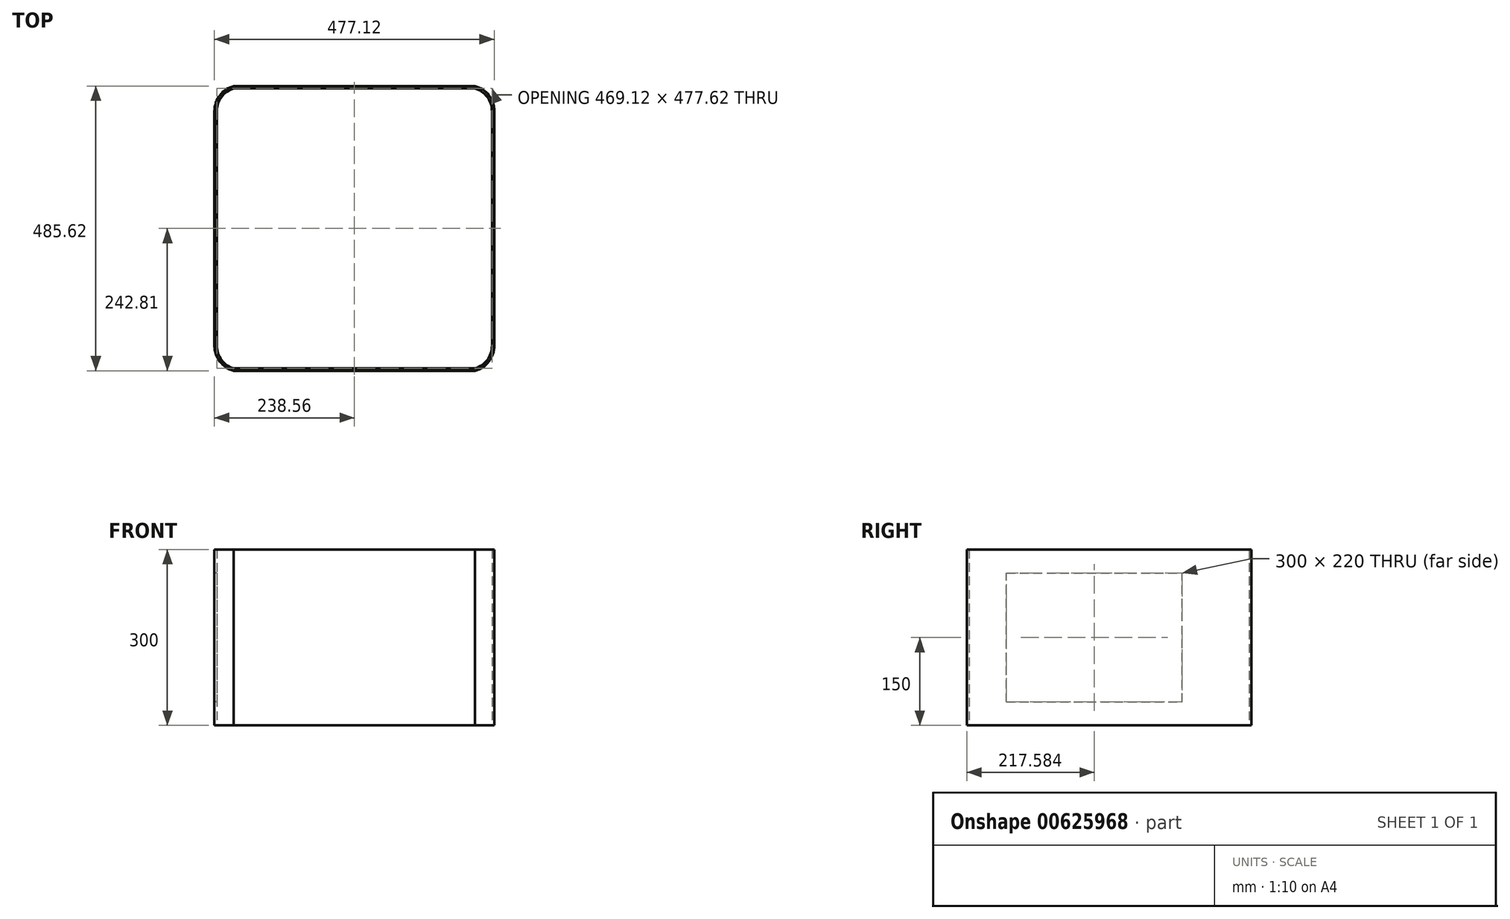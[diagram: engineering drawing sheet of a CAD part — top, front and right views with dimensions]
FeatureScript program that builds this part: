
annotation { "Feature Type Name" : "Feature", "Feature Type Description" : "" }
export const myFeature = defineFeature(function(context is Context, id is Id, definition is map)
    precondition{}
    {
        {
            var Q0;
            Q0=qCreatedBy(makeId("Top.planeOp"),FACE);
            var sketch = newSketch(context, id + "F0", { "sketchPlane" : qUnion([Q0])});
            skLineSegment(sketch, "E0.bottom", {"start": v(-205.64, 242.8) * mm, "end": v(205.63, 242.8) * mm});
            skLineSegment(sketch, "E0.top", {"start": v(-205.64, -242.8) * mm, "end": v(205.63, -242.8) * mm});
            skLineSegment(sketch, "E0.left", {"start": v(-238.56, 200.23) * mm, "end": v(-238.56, -200.23) * mm});
            skLineSegment(sketch, "E0.right", {"start": v(238.56, 200.23) * mm, "end": v(238.56, -200.23) * mm});
            skLineSegment(sketch, "E1", {"start": v(-205.64, 242.8) * mm, "end": v(205.63, 242.8) * mm, "construction": true});
            skLineSegment(sketch, "E2", {"start": v(-238.56, 200.23) * mm, "end": v(-238.56, -200.23) * mm, "construction": true});
            skLineSegment(sketch, "E3.MirrorCS", {"start": v(238.56, 200.23) * mm, "end": v(238.56, -200.23) * mm, "construction": true});
            skLineSegment(sketch, "E4.MirrorCS", {"start": v(-205.64, -242.8) * mm, "end": v(205.63, -242.8) * mm, "construction": true});
            skArc(sketch, "E5", {"start": v(-205.64, 242.8) * mm, "mid": v(-229.37, 227.14) * mm, "end": v(-238.56, 200.23) * mm});
            skArc(sketch, "E6", {"start": v(238.56, 200.23) * mm, "mid": v(229.37, 227.14) * mm, "end": v(205.63, 242.8) * mm});
            skArc(sketch, "E7", {"start": v(-238.56, -200.23) * mm, "mid": v(-229.37, -227.14) * mm, "end": v(-205.64, -242.8) * mm});
            skArc(sketch, "E8", {"start": v(205.63, -242.8) * mm, "mid": v(229.37, -227.14) * mm, "end": v(238.56, -200.23) * mm});
            skPoint(sketch, "E9.orphan", {"position": v(-238.56, 242.8) * mm});
            skPoint(sketch, "E10.orphan", {"position": v(-238.56, -242.8) * mm});
            skSolve(sketch);
        }
        {
            var Q0;
            Q0=makeQuery(id+"F0.imprint","IMPRINT",FACE,{"disambiguationData":[TD([[makeQuery(id+"F0.imprint","IMPRINT",EDGE,{"derivedFrom":sQuery(id+"F0.wireOp",EDGE,"E0.bottom")}),-1.0]])]});
            extrude(context, id + "F1", {"entities" : qUnion([Q0]), "depth" : 300 * mm, "offsetDistance" : 25 * mm});
        }
        {
            var Q0;
            Q0=makeQuery(id+"F1.opExtrude","CAP_FACE",FACE,{"disambiguationData":[OSD([sQuery(id+"F0.wireOp",EDGE,"E0.bottom"),sQuery(id+"F0.wireOp",EDGE,"E0.top"),sQuery(id+"F0.wireOp",EDGE,"E0.left"),sQuery(id+"F0.wireOp",EDGE,"E0.right"),sQuery(id+"F0.wireOp",EDGE,"E5"),sQuery(id+"F0.wireOp",EDGE,"E6"),sQuery(id+"F0.wireOp",EDGE,"E7"),sQuery(id+"F0.wireOp",EDGE,"E8")])],"isStart":true});
            shell(context, id + "F2", {"entities" : qUnion([Q0]), "thickness" : 4 * mm});
        }
        {
            var Q0;
            Q0=makeQuery(id+"F2.opShell","OFFSET_FACE",FACE,{"disambiguationData":[OSD([sQuery(id+"F0.wireOp",EDGE,"E0.bottom"),sQuery(id+"F0.wireOp",EDGE,"E0.top"),sQuery(id+"F0.wireOp",EDGE,"E0.left"),sQuery(id+"F0.wireOp",EDGE,"E0.right"),sQuery(id+"F0.wireOp",EDGE,"E5"),sQuery(id+"F0.wireOp",EDGE,"E6"),sQuery(id+"F0.wireOp",EDGE,"E7"),sQuery(id+"F0.wireOp",EDGE,"E8")])]});
            var sketch = newSketch(context, id + "F3", { "sketchPlane" : qUnion([Q0])});
            skLineSegment(sketch, "E11", {"start": v(-234.56, 200.23) * mm, "end": v(-234.56, -200.23) * mm});
            skArc(sketch, "E12", {"start": v(-234.56, -200.23) * mm, "mid": v(-226.36, -224.5) * mm, "end": v(-205.11, -238.8) * mm});
            skLineSegment(sketch, "E13", {"start": v(-205.11, -238.8) * mm, "end": v(205.11, -238.8) * mm});
            skArc(sketch, "E14", {"start": v(205.11, -238.8) * mm, "mid": v(226.36, -224.5) * mm, "end": v(234.56, -200.23) * mm});
            skLineSegment(sketch, "E15", {"start": v(234.56, -200.23) * mm, "end": v(234.56, 200.23) * mm});
            skArc(sketch, "E16", {"start": v(234.56, 200.23) * mm, "mid": v(226.36, 224.5) * mm, "end": v(205.11, 238.8) * mm});
            skLineSegment(sketch, "E17", {"start": v(205.11, 238.8) * mm, "end": v(-205.11, 238.8) * mm});
            skArc(sketch, "E18", {"start": v(-205.11, 238.8) * mm, "mid": v(-226.36, 224.5) * mm, "end": v(-234.56, 200.23) * mm});
            skSolve(sketch);
        }
        {
            var Q0;
            Q0=makeQuery(id+"F3.imprint","IMPRINT",FACE,{"disambiguationData":[TD([[makeQuery(id+"F3.imprint","IMPRINT",EDGE,{"derivedFrom":sQuery(id+"F3.wireOp",EDGE,"E11")}),-1.0]])]});
            extrude(context, id + "F4", {"entities" : qUnion([Q0]), "operationType" : NewBodyOperationType.REMOVE, "oppositeDirection" : true, "depth" : 25 * mm, "offsetDistance" : 25 * mm});
        }
        {
            var Q0;
            Q0=makeQuery(id+"F1.opExtrude","SWEPT_FACE",FACE,{"disambiguationData":[OSD([sQuery(id+"F0.wireOp",EDGE,"E0.left")])]});
            var sketch = newSketch(context, id + "F5", { "sketchPlane" : qUnion([Q0])});
            skLineSegment(sketch, "E19.bottom", {"start": v(175.23, 40) * mm, "end": v(-124.77, 40) * mm});
            skLineSegment(sketch, "E19.top", {"start": v(175.23, 260) * mm, "end": v(-124.77, 260) * mm});
            skLineSegment(sketch, "E19.left", {"start": v(175.23, 40) * mm, "end": v(175.23, 260) * mm});
            skLineSegment(sketch, "E19.right", {"start": v(-124.77, 40) * mm, "end": v(-124.77, 260) * mm});
            skSolve(sketch);
        }
        {
            var Q0;
            Q0=makeQuery(id+"F5.imprint","IMPRINT",FACE,{"disambiguationData":[TD([[makeQuery(id+"F5.imprint","IMPRINT",EDGE,{"derivedFrom":sQuery(id+"F5.wireOp",EDGE,"E19.bottom")}),-1.0]])]});
            extrude(context, id + "F6", {"entities" : qUnion([Q0]), "operationType" : NewBodyOperationType.REMOVE, "oppositeDirection" : true, "depth" : 25 * mm, "offsetDistance" : 25 * mm});
        }
    });
